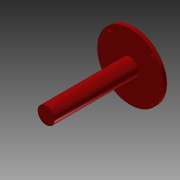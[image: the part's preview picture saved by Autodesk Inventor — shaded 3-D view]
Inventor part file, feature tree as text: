
AUTODESK INVENTOR PART (.ipt)
format: ipt  version: 2013 (Build 170138000, 138)  size: 100,352 bytes
history: native  units: mm
features: sketch x5, extrude x4, other x1, hole x1
ambient origin geometry x8: Origin, YZ Plane, XZ Plane, XY Plane, X Axis, Y Axis, Z Axis, Center Point
feature tree (11):
  other  "ソリッド1"
  extrude  "押し出し1"  Depth=14.0mm
  sketch  "スケッチ2"
  extrude  "押し出し2"  Depth=70.0mm TaperAngle=0.0deg
  extrude  "押し出し3"  Depth=55.0mm
  hole  "穴1"  [1 undecoded]
  extrude  "押し出し5"  Depth=3.0mm TaperAngle=0.0deg
  sketch  "スケッチ1"
  sketch  "スケッチ3"
  sketch  "スケッチ4"
  sketch  "スケッチ6"
note: 1 required parameter value undecoded (feature->parameter linkage not recoverable at this tier; creation-order binding heuristic only, values carry confidence <= 0.55)
